# Revit family: Storage-Secondary_Desks-Teknion-BSSP_Stretch_Pedestal-R2018
name_source: partatom
category: Furniture
revit_build: Autodesk Revit 2018 (Build: 20170223_1515(x64)
units: mm (PartAtom-declared; Revit-internal decimal feet)

## family parameters
Always vertical = Yes
Cut with Voids When Loaded = No
OmniClass Number = 23.40.20.00
OmniClass Title = General Furniture and Specialties
Room Calculation Point = No
Shared = Yes
Work Plane-Based = No

## types (4) — shared parameters
Assembly Code = E2020200
Manufacturer = Teknion
Manufacturer Fax = 416.661.4586
Part Number = BSSP
Product Documentation Link = http://www.teknion.com
Product Line = Expansion Casegoods
Product Page URL = http://www.teknion.com
Series = Expansion Casegoods
Sustainability Data = http://www.teknion.com
URL = www.teknion.com
Unit Weight URL = http://www.teknion.com
Warranty = http://www.teknion.com

## per-type parameters (varying)
| type | Description | Model | Width |
| Located at the End of a 1 3/16" Thick Secondary Desk, 18"w | Stretch Pedestal for Secondary Desk, End Position - 1 3/16" thick Secondary Desk, Not In Front of Height Adjustable Mechanism, High Seconday Desk Height, 18" Width | BSSPMNH__18 | 16.775 " |
| Located at the End of a 1" Thick Secondary Desk, 18"w | Stretch Pedestal for Secondary Desk, End Position - 1" thick Secondary Desk, Not In Front of Height Adjustable Mechanism, High Seconday Desk Height, 18" Width | BSSPDNH__18 | 16.775 " |
| Located at the End of a 1 9/16" Thick Secondary Desk, 18"w | Stretch Pedestal for Secondary Desk, End Position - 1 9/16" thick Secondary Desk, Not In Front of Height Adjustable Mechanism, High Seconday Desk Height, 18" Width | BSSPXNH__18 | 16.236 " |
| Located at the center of a Secondary Desk, 18"w | Stretch Pedestal for Secondary Desk, Center Position, Not In Front of Height Adjustable Mechanism, High Seconday Desk Height, 18" Width | BSSPCNH__18 | 17.91 " |

## geometry (parser evidence)
native form markers: Blend x142, Sweep x2
no freeform markers — native parametric forms only
